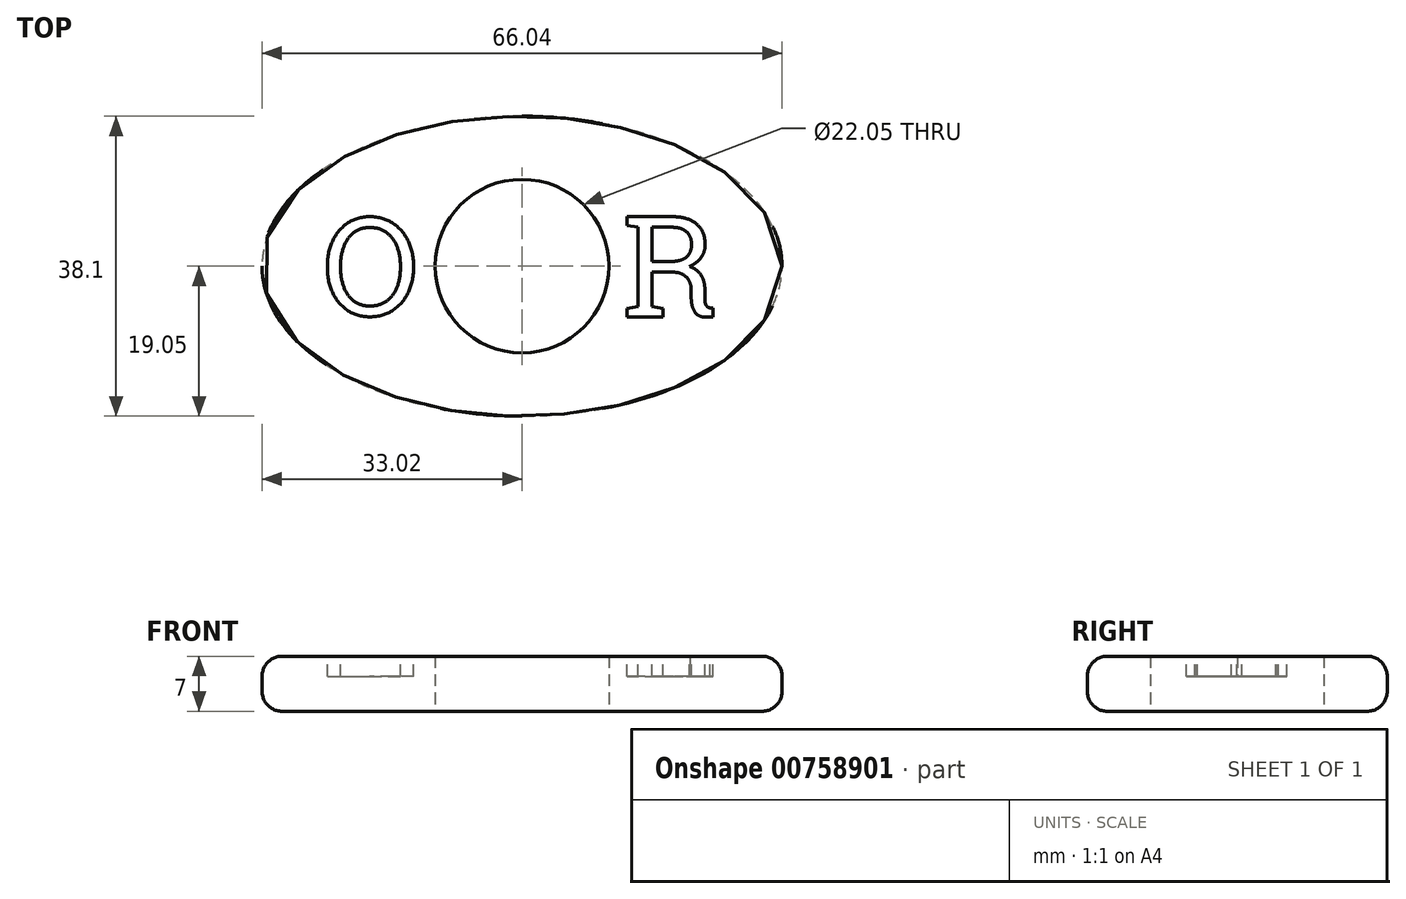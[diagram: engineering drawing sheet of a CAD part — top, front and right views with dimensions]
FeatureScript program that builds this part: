
annotation { "Feature Type Name" : "Feature", "Feature Type Description" : "" }
export const myFeature = defineFeature(function(context is Context, id is Id, definition is map)
    precondition{}
    {
        {
            var Q0;
            Q0=qCreatedBy(makeId("Top.planeOp"),FACE);
            var sketch = newSketch(context, id + "F0", { "sketchPlane" : qUnion([Q0])});
            skEllipse(sketch, "E0", {"center": v(0, 0) * mm, "majorRadius": 33.02 * mm, "minorRadius": 19.05 * mm, "majorAxis": v(1, 0)});
            skCircle(sketch, "E1", {"center": v(0, 0) * mm, "radius": 11.03 * mm});
            skLineSegment(sketch, "E2", {"start": v(-33.02, 0) * mm, "end": v(33.02, 0) * mm, "construction": true});
            skLineSegment(sketch, "E3", {"start": v(0, 19.05) * mm, "end": v(0, -19.05) * mm, "construction": true});
            skSolve(sketch);
        }
        {
            var Q0;
            Q0=makeQuery(id+"F0.imprint","IMPRINT",FACE,{"disambiguationData":[TD([[makeQuery(id+"F0.imprint","IMPRINT",EDGE,{"derivedFrom":sQuery(id+"F0.wireOp",EDGE,"E0")}),1.0]])]});
            extrude(context, id + "F1", {"entities" : qUnion([Q0]), "depth" : 7 * mm, "offsetDistance" : 25.4 * mm});
        }
        {
            var Q0;
            Q0=makeQuery(id+"F1.opExtrude","CAP_EDGE",EDGE,{"disambiguationData":[OSD([sQuery(id+"F0.wireOp",EDGE,"E0")])],"isStart":false});
            var Q1;
            Q1=makeQuery(id+"F1.opExtrude","CAP_EDGE",EDGE,{"disambiguationData":[OSD([sQuery(id+"F0.wireOp",EDGE,"E0")])],"isStart":true});
            fillet(context, id + "F2", {"entities" : qUnion([Q0, Q1]), "radius" : 2.54 * mm, "tangentPropagation" : true, "allowEdgeOverflow" : false});
        }
        {
            var Q0;
            Q0=makeQuery(id+"F1.opExtrude","CAP_FACE",FACE,{"disambiguationData":[OSD([sQuery(id+"F0.wireOp",EDGE,"E0"),sQuery(id+"F0.wireOp",EDGE,"E1")])],"isStart":false});
            var sketch = newSketch(context, id + "F3", { "sketchPlane" : qUnion([Q0])});
            skSolve(sketch);
        }
        {
            var Q0;
            {var subQ0=sQuery(id+"F0.wireOp",EDGE,"E1");Q0=makeQuery(id+"F3.imprint","IMPRINT",FACE,{"disambiguationData":[TD([[makeQuery(id+"F3.imprint","IMPRINT",EDGE,{"derivedFrom":makeQuery(id+"F1.opExtrude","CAP_EDGE",EDGE,{"disambiguationData":[OSD([subQ0])],"isStart":false})}),-1.0]])]});}
            var sketch = newSketch(context, id + "F4", { "sketchPlane" : qUnion([Q0])});
            skText(sketch, "E4", { "text": "O", "fontName": "RobotoSlab-Regular.ttf"});
            skText(sketch, "E5", { "text": "R", "fontName": "RobotoSlab-Regular.ttf"});
            skLineSegment(sketch, "E6", {"start": v(0, 0) * mm, "end": v(-25.4, 0) * mm, "construction": true});
            skLineSegment(sketch, "E7", {"start": v(0, 0) * mm, "end": v(25.4, 0) * mm, "construction": true});
            skLineSegment(sketch, "E8", {"start": v(-25.4, 0) * mm, "end": v(-12.7, 0) * mm, "construction": true});
            skLineSegment(sketch, "E9", {"start": v(12.7, 0) * mm, "end": v(25.4, 0) * mm});
            skPoint(sketch, "E10", {"position": v(19.05, 0) * mm});
            skLineSegment(sketch, "E11", {"start": v(12.7, 0) * mm, "end": v(25.4, 0) * mm, "construction": true});
            skPoint(sketch, "E12", {"position": v(-19.05, 0) * mm});
            const initialGuessF4  = {"E4": [-0.0254, -0.00626, 1, 0, 0.01253], "E5": [0.0127, -0.00648, 1, 0, 0.01295]};
            skSetInitialGuess(sketch, initialGuessF4);
            skSolve(sketch);
        }
        {
            var Q0;
            Q0=qSketchRegion(id+"F4",true);
            extrude(context, id + "F5", {"entities" : qUnion([Q0]), "operationType" : NewBodyOperationType.REMOVE, "oppositeDirection" : true, "depth" : 2.54 * mm, "offsetDistance" : 25.4 * mm});
        }
    });
